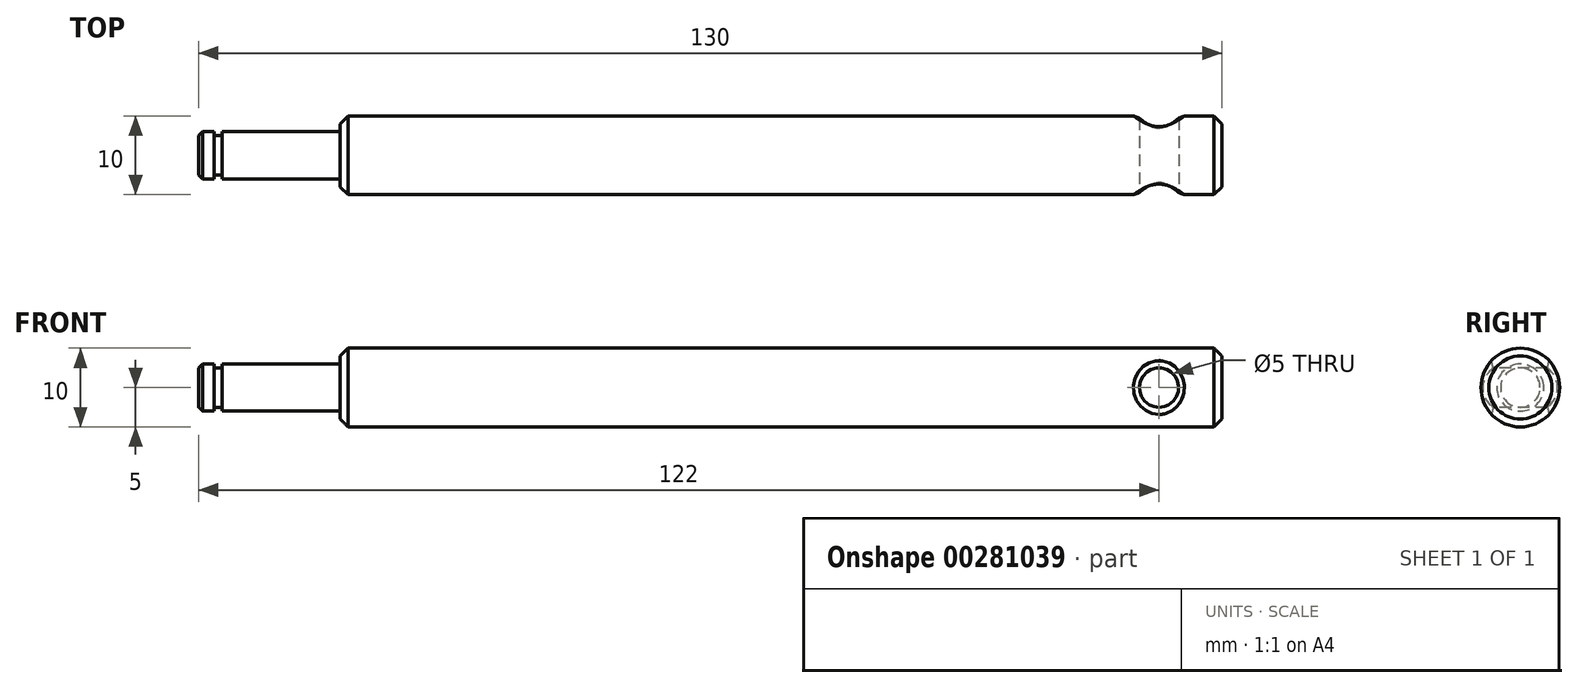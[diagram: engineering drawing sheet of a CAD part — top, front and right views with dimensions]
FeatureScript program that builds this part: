
annotation { "Feature Type Name" : "Feature", "Feature Type Description" : "" }
export const myFeature = defineFeature(function(context is Context, id is Id, definition is map)
    precondition{}
    {
        {
            var Q0;
            Q0=qCreatedBy(makeId("Front.planeOp"),FACE);
            var sketch = newSketch(context, id + "F0", { "sketchPlane" : qUnion([Q0])});
            skLineSegment(sketch, "E0", {"start": v(-65, 0) * mm, "end": v(-65, -3) * mm});
            skLineSegment(sketch, "E1", {"start": v(-65, -3) * mm, "end": v(-63, -3) * mm});
            skLineSegment(sketch, "E2", {"start": v(-63, -3) * mm, "end": v(-63, -2.5) * mm});
            skLineSegment(sketch, "E3", {"start": v(-63, -2.5) * mm, "end": v(-62, -2.5) * mm});
            skLineSegment(sketch, "E4", {"start": v(-62, -2.5) * mm, "end": v(-62, -3) * mm});
            skLineSegment(sketch, "E5", {"start": v(-62, -3) * mm, "end": v(-47, -3) * mm});
            skLineSegment(sketch, "E6", {"start": v(-47, -3) * mm, "end": v(-47, -5) * mm});
            skLineSegment(sketch, "E7", {"start": v(-47, -5) * mm, "end": v(65, -5) * mm});
            skLineSegment(sketch, "E8", {"start": v(65, -5) * mm, "end": v(65, 0) * mm});
            skLineSegment(sketch, "E9", {"start": v(65, 0) * mm, "end": v(-65, 0) * mm});
            skLineSegment(sketch, "E10", {"start": v(0, 0) * mm, "end": v(-16.9, 0) * mm, "construction": true});
            skSolve(sketch);
        }
        {
            var Q0;
            Q0=makeQuery(id+"F0.imprint","IMPRINT",FACE,{"disambiguationData":[TD([[makeQuery(id+"F0.imprint","IMPRINT",EDGE,{"derivedFrom":sQuery(id+"F0.wireOp",EDGE,"E0")}),1.0]])]});
            var Q1;
            Q1=sQuery(id+"F0.wireOp",EDGE,"E9");
            revolve(context, id + "F1", {"entities" : qUnion([Q0]), "axis" : qUnion([Q1]), "revolveType" : RevolveType.FULL});
        }
        {
            var Q0;
            Q0=makeQuery(id+"F1.opRevolve","SWEPT_EDGE",EDGE,{"disambiguationData":[OSD([sQuery(id+"F0.wireOp",EDGE,"E0"),sQuery(id+"F0.wireOp",EDGE,"E1")])]});
            chamfer(context, id + "F2", {"entities" : qUnion([Q0]), "chamferType" : ChamferType.OFFSET_ANGLE, "width" : .5 * mm, "oppositeDirection" : false, "angle" : 45 * degree, "tangentPropagation" : true});
        }
        {
            var Q0;
            Q0=makeQuery(id+"F1.opRevolve","SWEPT_EDGE",EDGE,{"disambiguationData":[OSD([sQuery(id+"F0.wireOp",EDGE,"E6"),sQuery(id+"F0.wireOp",EDGE,"E7")])]});
            var Q1;
            Q1=makeQuery(id+"F1.opRevolve","SWEPT_EDGE",EDGE,{"disambiguationData":[OSD([sQuery(id+"F0.wireOp",EDGE,"E7"),sQuery(id+"F0.wireOp",EDGE,"E8")])]});
            chamfer(context, id + "F3", {"entities" : qUnion([Q0, Q1]), "chamferType" : ChamferType.OFFSET_ANGLE, "width" : 1 * mm, "oppositeDirection" : false, "angle" : 45 * degree, "tangentPropagation" : true});
        }
        {
            var Q0;
            Q0=qCreatedBy(makeId("Front.planeOp"),FACE);
            var sketch = newSketch(context, id + "F4", { "sketchPlane" : qUnion([Q0])});
            skLineSegment(sketch, "E11", {"start": v(0, 0) * mm, "end": v(69.15, 0) * mm, "construction": true});
            skLineSegment(sketch, "E12.0", {"start": v(65, 4) * mm, "end": v(65, -4) * mm, "construction": true});
            skCircle(sketch, "E13", {"center": v(57, 0) * mm, "radius": 2.5 * mm});
            skSolve(sketch);
        }
        {
            var Q0;
            Q0 = qSketchRegion(id + "F4", true);
            extrude(context, id + "F5", {"entities" : qUnion([Q0]), "operationType" : NewBodyOperationType.REMOVE, "endBound" : BoundingType.SYMMETRIC, "oppositeDirection" : true, "depth" : 25 * mm});
        }
        {
            var Q0;
            Q0=makeQuery(id+"F5.boolean.opBoolean","COPY",FACE,{"derivedFrom":makeQuery(id+"F5.opExtrude","SWEPT_FACE",FACE,{"disambiguationData":[OSD([sQuery(id+"F4.wireOp",EDGE,"E13")])]})});
            chamfer(context, id + "F6", {"entities" : qUnion([Q0]), "chamferType" : ChamferType.OFFSET_ANGLE, "width" : 1 * mm, "oppositeDirection" : false, "angle" : 45 * degree, "tangentPropagation" : true});
        }
    });
